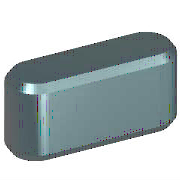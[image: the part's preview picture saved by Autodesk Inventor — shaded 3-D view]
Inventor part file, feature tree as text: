
AUTODESK INVENTOR PART (.ipt)
format: ipt  version: 2025 (Build 290162000, 162)  size: 139,264 bytes
history: native  units: mm (DEFAULTED — no unit token found)
features: plane x3, extrude x1
ambient origin geometry x8: Origin, YZ Plane, XZ Plane, XY Plane, X Axis, Y Axis, Z Axis, Center Point
bodies: Solid1 (feature_tree)
feature tree (4):
  plane  "Work Plane1"
  plane  "Work Plane2"
  extrude  "轴承体1"  Depth=9.0mm
  plane  "Work Plane3"
